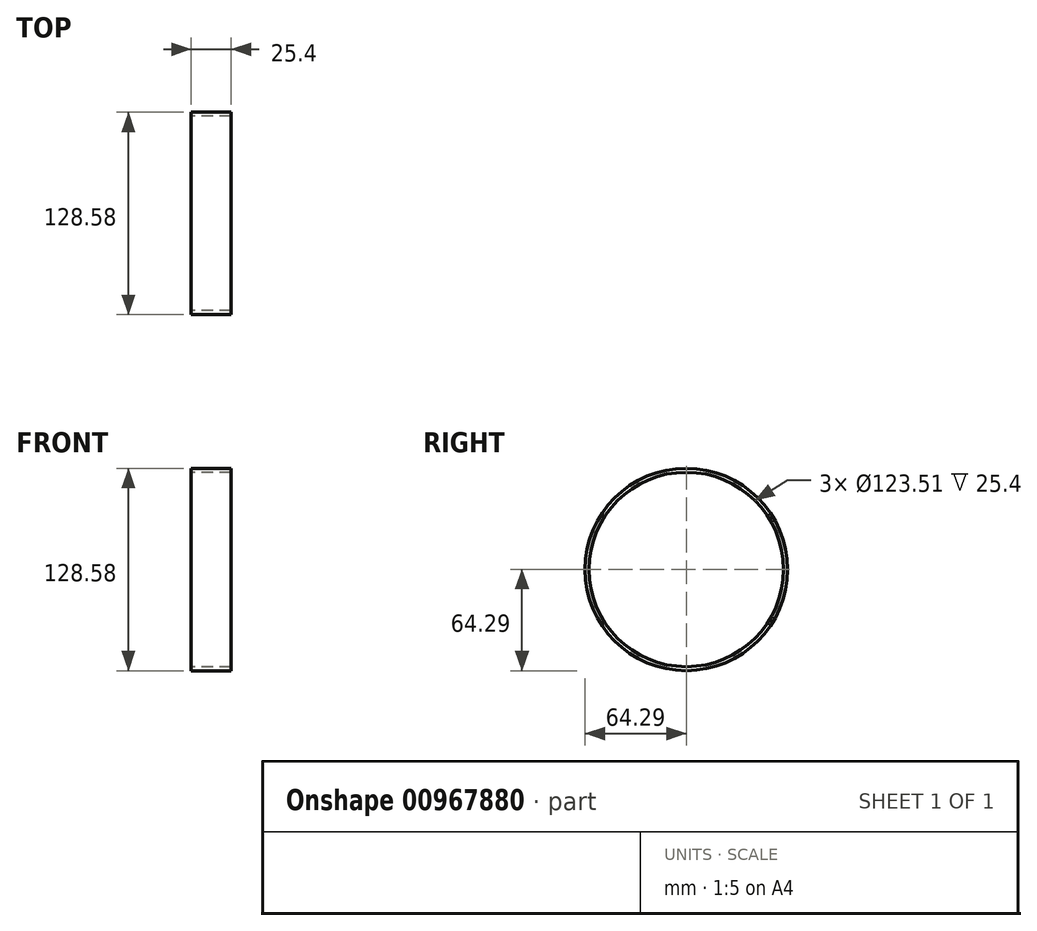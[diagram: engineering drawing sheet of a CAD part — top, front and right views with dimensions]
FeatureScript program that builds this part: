
annotation { "Feature Type Name" : "Feature", "Feature Type Description" : "" }
export const myFeature = defineFeature(function(context is Context, id is Id, definition is map)
    precondition{}
    {
        {
            var Q0;
            Q0=qCreatedBy(makeId("Right.planeOp"),FACE);
            var sketch = newSketch(context, id + "F0", { "sketchPlane" : qUnion([Q0])});
            skCircle(sketch, "E0", {"center": v(0, 0) * mm, "radius": 64.3 * mm});
            skCircle(sketch, "E1", {"center": v(0, 0) * mm, "radius": 61.75 * mm});
            skPoint(sketch, "E2", {"position": v(0, 61.75) * mm});
            skPoint(sketch, "E3", {"position": v(0, 64.3) * mm});
            skSolve(sketch);
        }
        {
            var Q0;
            Q0=makeQuery(id+"F0.imprint","IMPRINT",FACE,{"disambiguationData":[TD([[makeQuery(id+"F0.imprint","IMPRINT",EDGE,{"derivedFrom":sQuery(id+"F0.wireOp",EDGE,"E0")}),1.0]])]});
            extrude(context, id + "F1", {"entities" : qUnion([Q0]), "endBound" : BoundingType.SYMMETRIC, "depth" : 25.4 * mm, "offsetDistance" : 25.4 * mm});
        }
    });
